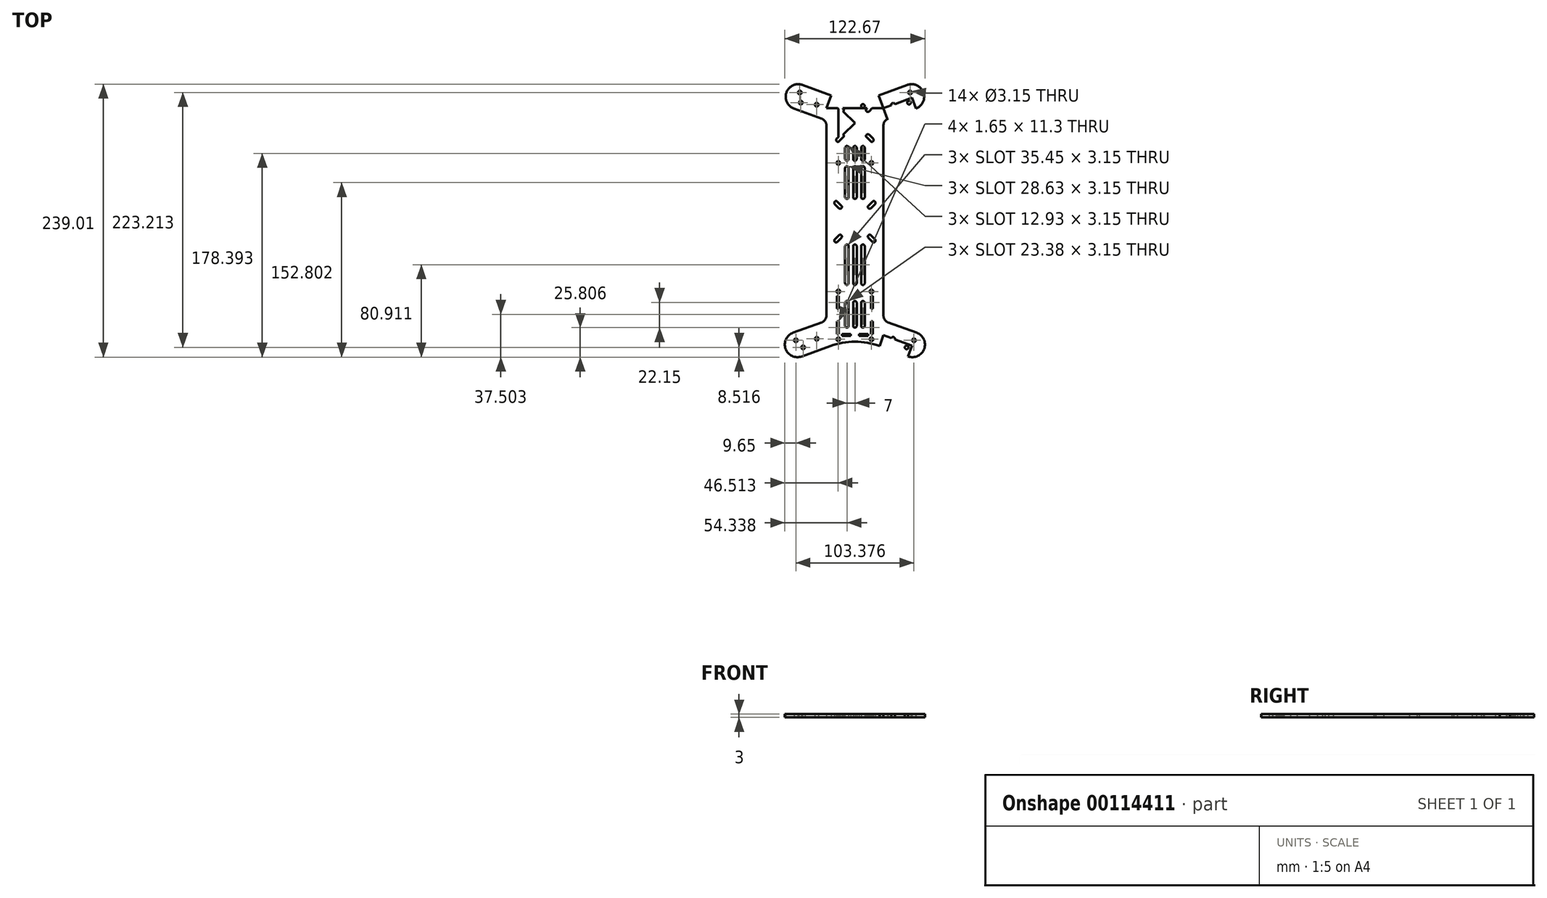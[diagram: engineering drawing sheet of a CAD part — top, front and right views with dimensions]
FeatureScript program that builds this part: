
annotation { "Feature Type Name" : "Feature", "Feature Type Description" : "" }
export const myFeature = defineFeature(function(context is Context, id is Id, definition is map)
    precondition{}
    {
        {
            var Q0;
            Q0=qCreatedBy(makeId("Top.planeOp"),FACE);
            var sketch = newSketch(context, id + "F0", { "sketchPlane" : qUnion([Q0])});
            skPoint(sketch, "E0.middle", {"position": v(0, 0) * mm});
            skLineSegment(sketch, "E1", {"start": v(4.78, 118.28) * mm, "end": v(4.78, 73.81) * mm});
            skCircle(sketch, "E2.MirrorC", {"center": v(56.47, -84.97) * mm, "radius": 1.57 * mm});
            skCircle(sketch, "E3.MirrorC", {"center": v(50.07, -91.17) * mm, "radius": 1.57 * mm});
            skCircle(sketch, "E4.MirrorC", {"center": v(38.24, -83.61) * mm, "radius": 1.57 * mm});
            skLineSegment(sketch, "E5", {"start": v(50.07, -91.17) * mm, "end": v(51.12, -88.3) * mm});
            skLineSegment(sketch, "E6", {"start": v(56.47, -84.97) * mm, "end": v(54.77, -89.63) * mm});
            skLineSegment(sketch, "E7", {"start": v(54.77, -89.63) * mm, "end": v(29.78, -80.53) * mm});
            skCircle(sketch, "E8.MirrorC", {"center": v(53.07, 132.04) * mm, "radius": 1.57 * mm});
            skCircle(sketch, "E9.MirrorC", {"center": v(52.16, 123.17) * mm, "radius": 1.57 * mm});
            skCircle(sketch, "E10.MirrorC", {"center": v(38.24, 121.36) * mm, "radius": 1.57 * mm});
            skLineSegment(sketch, "E11", {"start": v(52.16, 123.17) * mm, "end": v(51.12, 126.05) * mm});
            skLineSegment(sketch, "E12", {"start": v(50.67, 138.65) * mm, "end": v(53.07, 132.04) * mm});
            skLineSegment(sketch, "E13", {"start": v(54.77, 127.38) * mm, "end": v(29.78, 118.28) * mm});
            skLineSegment(sketch, "E14", {"start": v(29.78, 118.28) * mm, "end": v(4.78, 118.28) * mm});
            skLineSegment(sketch, "E15", {"start": v(29.78, -80.53) * mm, "end": v(4.78, -80.53) * mm});
            skLineSegment(sketch, "E16.bottom", {"start": v(21.28, 35.37) * mm, "end": v(4.78, 35.37) * mm});
            skLineSegment(sketch, "E16.top", {"start": v(21.28, 2.37) * mm, "end": v(4.78, 2.37) * mm});
            skLineSegment(sketch, "E16.left", {"start": v(21.28, 35.37) * mm, "end": v(21.28, 2.37) * mm});
            skLineSegment(sketch, "E17", {"start": v(29.78, 118.28) * mm, "end": v(29.78, -80.53) * mm});
            skCircle(sketch, "E18", {"center": v(21.28, 35.37) * mm, "radius": 1.58 * mm});
            skCircle(sketch, "E19", {"center": v(21.28, 2.37) * mm, "radius": 1.58 * mm});
            skLineSegment(sketch, "E20", {"start": v(4.78, 18.87) * mm, "end": v(21.28, 35.37) * mm});
            skLineSegment(sketch, "E21", {"start": v(4.78, 18.87) * mm, "end": v(21.28, 2.37) * mm});
            skPoint(sketch, "E22", {"position": v(17.74, 31.84) * mm});
            skPoint(sketch, "E23.MirrorP", {"position": v(17.74, 5.9) * mm});
            skCircle(sketch, "E24", {"center": v(17.74, 31.84) * mm, "radius": 1.58 * mm});
            skLineSegment(sketch, "E25", {"start": v(17.74, 31.84) * mm, "end": v(18.86, 30.72) * mm});
            skLineSegment(sketch, "E26", {"start": v(18.86, 30.72) * mm, "end": v(17.74, 31.84) * mm});
            skLineSegment(sketch, "E27", {"start": v(17.74, 31.84) * mm, "end": v(16.63, 32.95) * mm});
            skLineSegment(sketch, "E28", {"start": v(21.28, 35.37) * mm, "end": v(22.4, 34.26) * mm});
            skLineSegment(sketch, "E29", {"start": v(22.4, 34.26) * mm, "end": v(18.86, 30.72) * mm});
            skLineSegment(sketch, "E30", {"start": v(21.28, 35.37) * mm, "end": v(20.16, 36.49) * mm});
            skLineSegment(sketch, "E31", {"start": v(20.16, 36.49) * mm, "end": v(16.63, 32.95) * mm});
            skLineSegment(sketch, "E32", {"start": v(21.28, 2.37) * mm, "end": v(22.4, 3.49) * mm});
            skLineSegment(sketch, "E33", {"start": v(21.28, 2.37) * mm, "end": v(20.16, 1.26) * mm});
            skCircle(sketch, "E34", {"center": v(17.74, 5.9) * mm, "radius": 1.57 * mm});
            skLineSegment(sketch, "E35", {"start": v(17.74, 5.9) * mm, "end": v(16.63, 4.8) * mm});
            skLineSegment(sketch, "E36", {"start": v(16.63, 4.8) * mm, "end": v(20.16, 1.26) * mm});
            skLineSegment(sketch, "E37", {"start": v(17.74, 5.9) * mm, "end": v(18.86, 7.02) * mm});
            skLineSegment(sketch, "E38", {"start": v(18.86, 7.02) * mm, "end": v(22.4, 3.49) * mm});
            skLineSegment(sketch, "E39", {"start": v(58.87, -78.35) * mm, "end": v(33.88, -69.26) * mm});
            skLineSegment(sketch, "E40", {"start": v(51.35, -99.03) * mm, "end": v(26.36, -89.93) * mm});
            skLineSegment(sketch, "E41", {"start": v(33.88, -69.26) * mm, "end": v(29.78, -80.53) * mm});
            skLineSegment(sketch, "E42", {"start": v(29.78, -80.53) * mm, "end": v(26.36, -89.93) * mm});
            skLineSegment(sketch, "E43.MirrorCS", {"start": v(33.2, 108.88) * mm, "end": v(29.78, 118.28) * mm});
            skLineSegment(sketch, "E44", {"start": v(54.77, 127.38) * mm, "end": v(58.2, 117.98) * mm});
            skLineSegment(sketch, "E45", {"start": v(53.07, 132.04) * mm, "end": v(54.77, 127.38) * mm});
            skLineSegment(sketch, "E46", {"start": v(54.77, -89.63) * mm, "end": v(51.35, -99.03) * mm});
            skLineSegment(sketch, "E47", {"start": v(56.47, -84.97) * mm, "end": v(58.87, -78.35) * mm});
            skArc(sketch, "E48", {"start": v(51.35, -99.03) * mm, "mid": v(65.45, -92.45) * mm, "end": v(58.87, -78.35) * mm});
            skLineSegment(sketch, "E49.top", {"start": v(4.78, -46.08) * mm, "end": v(18.78, -46.08) * mm});
            skLineSegment(sketch, "E49.right", {"start": v(18.78, -79.53) * mm, "end": v(18.78, -46.08) * mm});
            skLineSegment(sketch, "E50", {"start": v(18.78, -46.08) * mm, "end": v(20.43, -46.08) * mm});
            skLineSegment(sketch, "E51", {"start": v(20.43, -46.08) * mm, "end": v(20.43, -57.38) * mm});
            skLineSegment(sketch, "E52", {"start": v(20.43, -57.38) * mm, "end": v(18.78, -57.38) * mm});
            skLineSegment(sketch, "E53.bottom", {"start": v(9.78, 110.28) * mm, "end": v(4.78, 110.28) * mm});
            skLineSegment(sketch, "E53.top", {"start": v(9.78, 100.28) * mm, "end": v(4.78, 100.28) * mm});
            skLineSegment(sketch, "E53.left", {"start": v(9.78, 110.28) * mm, "end": v(9.78, 100.28) * mm});
            skLineSegment(sketch, "E53.right", {"start": v(-0.22, 110.28) * mm, "end": v(-0.22, 100.28) * mm});
            skLineSegment(sketch, "E54", {"start": v(4.78, 105.28) * mm, "end": v(19.63, 120.13) * mm});
            skLineSegment(sketch, "E55", {"start": v(4.78, 105.28) * mm, "end": v(19.63, 90.43) * mm});
            skCircle(sketch, "E56", {"center": v(19.63, 120.13) * mm, "radius": 1.57 * mm});
            skCircle(sketch, "E57", {"center": v(19.63, 90.43) * mm, "radius": 1.57 * mm});
            skPoint(sketch, "E58", {"position": v(16.1, 116.6) * mm});
            skPoint(sketch, "E59", {"position": v(16.1, 93.97) * mm});
            skCircle(sketch, "E60", {"center": v(16.1, 116.6) * mm, "radius": 1.58 * mm});
            skLineSegment(sketch, "E61", {"start": v(19.63, 120.13) * mm, "end": v(20.74, 119.02) * mm});
            skLineSegment(sketch, "E62", {"start": v(19.63, 120.13) * mm, "end": v(18.51, 121.24) * mm});
            skLineSegment(sketch, "E63", {"start": v(16.1, 116.6) * mm, "end": v(17.2, 115.48) * mm});
            skLineSegment(sketch, "E64", {"start": v(17.2, 115.48) * mm, "end": v(20.74, 119.02) * mm});
            skLineSegment(sketch, "E65", {"start": v(16.1, 116.6) * mm, "end": v(14.98, 117.7) * mm});
            skLineSegment(sketch, "E66", {"start": v(14.98, 117.7) * mm, "end": v(18.51, 121.24) * mm});
            skCircle(sketch, "E67", {"center": v(16.1, 93.97) * mm, "radius": 1.58 * mm});
            skLineSegment(sketch, "E68", {"start": v(16.1, 93.97) * mm, "end": v(14.98, 92.85) * mm});
            skLineSegment(sketch, "E69", {"start": v(16.1, 93.97) * mm, "end": v(17.2, 95.08) * mm});
            skLineSegment(sketch, "E70", {"start": v(19.63, 90.43) * mm, "end": v(18.51, 89.32) * mm});
            skLineSegment(sketch, "E71", {"start": v(18.51, 89.32) * mm, "end": v(14.98, 92.85) * mm});
            skLineSegment(sketch, "E72", {"start": v(19.63, 90.43) * mm, "end": v(20.74, 91.55) * mm});
            skLineSegment(sketch, "E73", {"start": v(20.74, 91.55) * mm, "end": v(17.2, 95.08) * mm});
            skLineSegment(sketch, "E74", {"start": v(33.88, -69.26) * mm, "end": v(29.78, -67.76) * mm});
            skArc(sketch, "E75", {"start": v(33.88, -69.26) * mm, "mid": v(30.9, -66.97) * mm, "end": v(29.78, -63.4) * mm});
            skArc(sketch, "E76", {"start": v(26.36, -89.93) * mm, "mid": v(15.73, -87.08) * mm, "end": v(4.78, -86.13) * mm});
            skPoint(sketch, "E77", {"position": v(4.78, -86.13) * mm});
            skLineSegment(sketch, "E78", {"start": v(18.78, -68.23) * mm, "end": v(20.43, -68.23) * mm});
            skLineSegment(sketch, "E79", {"start": v(18.78, -79.53) * mm, "end": v(20.43, -79.53) * mm});
            skLineSegment(sketch, "E80", {"start": v(20.43, -79.53) * mm, "end": v(20.43, -68.23) * mm});
            skLineSegment(sketch, "E81", {"start": v(19.28, -79.53) * mm, "end": v(19.28, -84.03) * mm});
            skCircle(sketch, "E82", {"center": v(19.28, -84.03) * mm, "radius": 1.57 * mm});
            skLineSegment(sketch, "E83", {"start": v(19.28, -79.53) * mm, "end": v(19.28, -42.18) * mm});
            skCircle(sketch, "E84", {"center": v(19.28, -42.18) * mm, "radius": 1.57 * mm});
            skCircle(sketch, "E85.MirrorC", {"center": v(11.78, 120.28) * mm, "radius": 1.57 * mm});
            skLineSegment(sketch, "E86.MirrorCS", {"start": v(11.78, 118.28) * mm, "end": v(11.78, 120.28) * mm});
            skLineSegment(sketch, "E87", {"start": v(19.28, -42.18) * mm, "end": v(19.28, 118.28) * mm});
            skCircle(sketch, "E88", {"center": v(19.28, 70.37) * mm, "radius": 1.57 * mm});
            skLineSegment(sketch, "E89", {"start": v(4.78, -79.53) * mm, "end": v(4.78, -80.53) * mm});
            skLineSegment(sketch, "E90.trimOffspring", {"start": v(4.78, -79.53) * mm, "end": v(18.78, -79.53) * mm});
            skLineSegment(sketch, "E91.trimOffspring", {"start": v(4.78, 18.87) * mm, "end": v(29.78, 18.87) * mm});
            skLineSegment(sketch, "E92.MirrorCS", {"start": v(-8.19, 31.84) * mm, "end": v(-9.3, 30.72) * mm});
            skLineSegment(sketch, "E93.MirrorCS", {"start": v(-9.3, 30.72) * mm, "end": v(-8.19, 31.84) * mm});
            skLineSegment(sketch, "E94.MirrorCS", {"start": v(-11.72, 35.37) * mm, "end": v(-12.84, 34.26) * mm});
            skLineSegment(sketch, "E95.MirrorCS", {"start": v(-12.84, 34.26) * mm, "end": v(-9.3, 30.72) * mm});
            skLineSegment(sketch, "E96.MirrorCS", {"start": v(-11.72, 35.37) * mm, "end": v(-10.6, 36.49) * mm});
            skLineSegment(sketch, "E97.MirrorCS", {"start": v(-8.19, 31.84) * mm, "end": v(-7.07, 32.95) * mm});
            skCircle(sketch, "E98.MirrorC", {"center": v(-11.72, 35.37) * mm, "radius": 1.58 * mm});
            skLineSegment(sketch, "E99.MirrorCS", {"start": v(-10.6, 36.49) * mm, "end": v(-7.07, 32.95) * mm});
            skCircle(sketch, "E100.MirrorC", {"center": v(-8.19, 31.84) * mm, "radius": 1.58 * mm});
            skLineSegment(sketch, "E101.MirrorCS", {"start": v(-10.07, 120.13) * mm, "end": v(-11.18, 119.02) * mm});
            skLineSegment(sketch, "E102.MirrorCS", {"start": v(-10.07, 90.43) * mm, "end": v(-8.96, 89.32) * mm});
            skLineSegment(sketch, "E103.MirrorCS", {"start": v(-6.54, 93.97) * mm, "end": v(-7.65, 95.08) * mm});
            skLineSegment(sketch, "E104.MirrorCS", {"start": v(-6.54, 116.6) * mm, "end": v(-7.65, 115.48) * mm});
            skLineSegment(sketch, "E105.MirrorCS", {"start": v(-10.07, 120.13) * mm, "end": v(-8.96, 121.24) * mm});
            skLineSegment(sketch, "E106.MirrorCS", {"start": v(-11.72, 2.37) * mm, "end": v(-10.6, 1.26) * mm});
            skLineSegment(sketch, "E107.MirrorCS", {"start": v(-7.07, 4.8) * mm, "end": v(-10.6, 1.26) * mm});
            skLineSegment(sketch, "E108.MirrorCS", {"start": v(-11.72, 2.37) * mm, "end": v(-12.84, 3.49) * mm});
            skLineSegment(sketch, "E109.MirrorCS", {"start": v(-9.3, 7.02) * mm, "end": v(-12.84, 3.49) * mm});
            skCircle(sketch, "E110.MirrorC", {"center": v(-10.07, 120.13) * mm, "radius": 1.57 * mm});
            skCircle(sketch, "E111.MirrorC", {"center": v(-10.07, 90.43) * mm, "radius": 1.57 * mm});
            skLineSegment(sketch, "E112.MirrorCS", {"start": v(-5.42, 117.7) * mm, "end": v(-8.96, 121.24) * mm});
            skCircle(sketch, "E113.MirrorC", {"center": v(-11.72, 2.37) * mm, "radius": 1.58 * mm});
            skLineSegment(sketch, "E114.MirrorCS", {"start": v(-11.18, 91.55) * mm, "end": v(-7.65, 95.08) * mm});
            skLineSegment(sketch, "E115.MirrorCS", {"start": v(-8.96, 89.32) * mm, "end": v(-5.42, 92.85) * mm});
            skLineSegment(sketch, "E116.MirrorCS", {"start": v(-6.54, 116.6) * mm, "end": v(-5.42, 117.7) * mm});
            skLineSegment(sketch, "E117.MirrorCS", {"start": v(-9.22, -79.53) * mm, "end": v(-10.87, -79.53) * mm});
            skCircle(sketch, "E118.MirrorC", {"center": v(-6.54, 116.6) * mm, "radius": 1.58 * mm});
            skLineSegment(sketch, "E119.MirrorCS", {"start": v(-7.65, 115.48) * mm, "end": v(-11.18, 119.02) * mm});
            skLineSegment(sketch, "E120.MirrorCS", {"start": v(-6.54, 93.97) * mm, "end": v(-5.42, 92.85) * mm});
            skLineSegment(sketch, "E121.MirrorCS", {"start": v(-9.72, -79.53) * mm, "end": v(-9.72, -84.03) * mm});
            skCircle(sketch, "E122.MirrorC", {"center": v(-6.54, 93.97) * mm, "radius": 1.58 * mm});
            skLineSegment(sketch, "E123.MirrorCS", {"start": v(-10.07, 90.43) * mm, "end": v(-11.18, 91.55) * mm});
            skLineSegment(sketch, "E124.MirrorCS", {"start": v(-8.19, 5.9) * mm, "end": v(-9.3, 7.02) * mm});
            skLineSegment(sketch, "E125.MirrorCS", {"start": v(-42.6, 123.17) * mm, "end": v(-41.56, 126.05) * mm});
            skLineSegment(sketch, "E126.MirrorCS", {"start": v(-8.19, 5.9) * mm, "end": v(-7.07, 4.8) * mm});
            skLineSegment(sketch, "E127.MirrorCS", {"start": v(-24.33, -69.26) * mm, "end": v(-20.22, -67.76) * mm});
            skLineSegment(sketch, "E128.MirrorCS", {"start": v(-46.9, -84.97) * mm, "end": v(-45.21, -89.63) * mm});
            skCircle(sketch, "E129.MirrorC", {"center": v(-8.19, 5.9) * mm, "radius": 1.57 * mm});
            skLineSegment(sketch, "E130.MirrorCS", {"start": v(-40.51, -91.17) * mm, "end": v(-41.56, -88.3) * mm});
            skLineSegment(sketch, "E131.MirrorCS", {"start": v(-43.52, 132.04) * mm, "end": v(-45.21, 127.38) * mm});
            skLineSegment(sketch, "E132.MirrorCS", {"start": v(-24.33, -69.26) * mm, "end": v(-20.22, -80.53) * mm});
            skLineSegment(sketch, "E133.MirrorCS", {"start": v(-46.9, -84.97) * mm, "end": v(-49.32, -78.35) * mm});
            skCircle(sketch, "E134.MirrorC", {"center": v(-46.9, -84.97) * mm, "radius": 1.57 * mm});
            skLineSegment(sketch, "E135.MirrorCS", {"start": v(-2.22, 118.28) * mm, "end": v(-2.22, 120.28) * mm});
            skLineSegment(sketch, "E136.MirrorCS", {"start": v(-41.1, 138.65) * mm, "end": v(-43.52, 132.04) * mm});
            skLineSegment(sketch, "E137.MirrorCS", {"start": v(-23.64, 108.88) * mm, "end": v(-20.22, 118.28) * mm});
            skCircle(sketch, "E138.MirrorC", {"center": v(-43.52, 132.04) * mm, "radius": 1.57 * mm});
            skLineSegment(sketch, "E139.MirrorCS", {"start": v(-45.21, 127.38) * mm, "end": v(-48.63, 117.98) * mm});
            skLineSegment(sketch, "E140.MirrorCS", {"start": v(-20.22, 118.28) * mm, "end": v(-16.12, 129.56) * mm});
            skLineSegment(sketch, "E141.MirrorCS", {"start": v(-9.22, -79.53) * mm, "end": v(-9.22, -46.08) * mm});
            skLineSegment(sketch, "E142.MirrorCS", {"start": v(-10.87, -79.53) * mm, "end": v(-10.87, -68.23) * mm});
            skCircle(sketch, "E143.MirrorC", {"center": v(-2.22, 120.28) * mm, "radius": 1.57 * mm});
            skLineSegment(sketch, "E144.MirrorCS", {"start": v(-45.21, -89.63) * mm, "end": v(-41.8, -99.03) * mm});
            skLineSegment(sketch, "E145.MirrorCS", {"start": v(-20.22, -80.53) * mm, "end": v(-16.8, -89.93) * mm});
            skLineSegment(sketch, "E146.MirrorCS", {"start": v(-9.22, -68.23) * mm, "end": v(-10.87, -68.23) * mm});
            skLineSegment(sketch, "E147.MirrorCS", {"start": v(-9.22, -46.08) * mm, "end": v(-10.87, -46.08) * mm});
            skCircle(sketch, "E148.MirrorC", {"center": v(-42.6, 123.17) * mm, "radius": 1.57 * mm});
            skCircle(sketch, "E149.MirrorC", {"center": v(-40.51, -91.17) * mm, "radius": 1.57 * mm});
            skCircle(sketch, "E150.MirrorC", {"center": v(-9.72, -42.18) * mm, "radius": 1.57 * mm});
            skCircle(sketch, "E151.MirrorC", {"center": v(-9.72, -84.03) * mm, "radius": 1.57 * mm});
            skLineSegment(sketch, "E152.MirrorCS", {"start": v(-9.72, -79.53) * mm, "end": v(-9.72, -42.18) * mm});
            skArc(sketch, "E153.MirrorCS", {"start": v(-24.33, -69.26) * mm, "mid": v(-21.35, -66.97) * mm, "end": v(-20.22, -63.4) * mm});
            skLineSegment(sketch, "E154.MirrorCS", {"start": v(-10.87, -57.38) * mm, "end": v(-9.22, -57.38) * mm});
            skLineSegment(sketch, "E155.MirrorCS", {"start": v(-10.87, -46.08) * mm, "end": v(-10.87, -57.38) * mm});
            skCircle(sketch, "E156.MirrorC", {"center": v(-28.68, 121.36) * mm, "radius": 1.57 * mm});
            skCircle(sketch, "E157.MirrorC", {"center": v(-28.68, -83.61) * mm, "radius": 1.57 * mm});
            skLineSegment(sketch, "E158.MirrorCS", {"start": v(-45.21, -89.63) * mm, "end": v(-20.22, -80.53) * mm});
            skCircle(sketch, "E159.MirrorC", {"center": v(-9.72, 70.37) * mm, "radius": 1.57 * mm});
            skLineSegment(sketch, "E160.MirrorCS", {"start": v(-45.21, 127.38) * mm, "end": v(-20.22, 118.28) * mm});
            skLineSegment(sketch, "E161.MirrorCS", {"start": v(-41.8, -99.03) * mm, "end": v(-16.8, -89.93) * mm});
            skLineSegment(sketch, "E162.MirrorCS", {"start": v(-49.32, -78.35) * mm, "end": v(-24.33, -69.26) * mm});
            skArc(sketch, "E163.MirrorCS", {"start": v(-41.8, -99.03) * mm, "mid": v(-55.9, -92.45) * mm, "end": v(-49.32, -78.35) * mm});
            skLineSegment(sketch, "E164.MirrorCS", {"start": v(-20.22, 118.28) * mm, "end": v(-20.22, -80.53) * mm});
            skLineSegment(sketch, "E165.MirrorCS", {"start": v(-9.72, -42.18) * mm, "end": v(-9.72, 118.28) * mm});
            skLineSegment(sketch, "E166.MirrorCS", {"start": v(-11.72, 35.37) * mm, "end": v(-11.72, 2.37) * mm});
            skLineSegment(sketch, "E167.MirrorCS", {"start": v(-0.22, 110.28) * mm, "end": v(4.78, 110.28) * mm});
            skLineSegment(sketch, "E168.MirrorCS", {"start": v(-0.22, 100.28) * mm, "end": v(4.78, 100.28) * mm});
            skLineSegment(sketch, "E169.MirrorCS", {"start": v(4.78, 105.28) * mm, "end": v(-10.07, 90.43) * mm});
            skLineSegment(sketch, "E170.MirrorCS", {"start": v(4.78, 105.28) * mm, "end": v(-10.07, 120.13) * mm});
            skLineSegment(sketch, "E171.MirrorCS", {"start": v(-20.22, 118.28) * mm, "end": v(4.78, 118.28) * mm});
            skLineSegment(sketch, "E172.MirrorCS", {"start": v(-11.72, 35.37) * mm, "end": v(4.78, 35.37) * mm});
            skLineSegment(sketch, "E173.MirrorCS", {"start": v(-11.72, 2.37) * mm, "end": v(4.78, 2.37) * mm});
            skLineSegment(sketch, "E174.MirrorCS", {"start": v(4.78, 18.87) * mm, "end": v(-20.22, 18.87) * mm});
            skLineSegment(sketch, "E175.MirrorCS", {"start": v(4.78, 18.87) * mm, "end": v(-11.72, 35.37) * mm});
            skLineSegment(sketch, "E176.MirrorCS", {"start": v(4.78, 18.87) * mm, "end": v(-11.72, 2.37) * mm});
            skLineSegment(sketch, "E177.MirrorCS", {"start": v(4.78, -46.08) * mm, "end": v(-9.22, -46.08) * mm});
            skArc(sketch, "E178.MirrorCS", {"start": v(-16.8, -89.93) * mm, "mid": v(-6.18, -87.08) * mm, "end": v(4.78, -86.13) * mm});
            skLineSegment(sketch, "E179.MirrorCS", {"start": v(4.78, -79.53) * mm, "end": v(-9.22, -79.53) * mm});
            skLineSegment(sketch, "E180.MirrorCS", {"start": v(-20.22, -80.53) * mm, "end": v(4.78, -80.53) * mm});
            skLineSegment(sketch, "E181", {"start": v(16.2, -81.18) * mm, "end": v(8.55, -81.18) * mm});
            skLineSegment(sketch, "E182", {"start": v(1, -81.18) * mm, "end": v(-6.65, -81.18) * mm});
            skLineSegment(sketch, "E183", {"start": v(16.2, -81.18) * mm, "end": v(16.2, -79.53) * mm});
            skLineSegment(sketch, "E184", {"start": v(8.55, -81.18) * mm, "end": v(8.55, -79.53) * mm});
            skLineSegment(sketch, "E185", {"start": v(1, -81.18) * mm, "end": v(1, -79.53) * mm});
            skLineSegment(sketch, "E186", {"start": v(-6.65, -81.18) * mm, "end": v(-6.65, -79.53) * mm});
            skLineSegment(sketch, "E187", {"start": v(29.78, 118.28) * mm, "end": v(25.67, 129.56) * mm});
            skLineSegment(sketch, "E188", {"start": v(-41.1, 138.65) * mm, "end": v(-16.12, 129.56) * mm});
            skLineSegment(sketch, "E189", {"start": v(50.67, 138.65) * mm, "end": v(25.67, 129.56) * mm});
            skArc(sketch, "E190", {"start": v(25.67, 129.56) * mm, "mid": v(4.78, 125.87) * mm, "end": v(-16.12, 129.56) * mm});
            skLineSegment(sketch, "E191", {"start": v(58.2, 117.98) * mm, "end": v(33.88, 109.13) * mm});
            skLineSegment(sketch, "E192", {"start": v(-23.64, 108.88) * mm, "end": v(-48.63, 117.98) * mm});
            skLineSegment(sketch, "E193", {"start": v(-23.64, 108.88) * mm, "end": v(-20.22, 107.64) * mm});
            skLineSegment(sketch, "E194", {"start": v(33.2, 108.88) * mm, "end": v(29.78, 107.64) * mm});
            skArc(sketch, "E195", {"start": v(58.2, 117.98) * mm, "mid": v(64.76, 132.08) * mm, "end": v(50.67, 138.65) * mm});
            skArc(sketch, "E196", {"start": v(-48.63, 117.98) * mm, "mid": v(-55.2, 132.08) * mm, "end": v(-41.1, 138.65) * mm});
            skPoint(sketch, "E197", {"position": v(29.78, 103.27) * mm});
            skPoint(sketch, "E198", {"position": v(33.88, 109.13) * mm});
            skArc(sketch, "E199", {"start": v(33.88, 109.13) * mm, "mid": v(30.9, 106.85) * mm, "end": v(29.78, 103.27) * mm});
            skLineSegment(sketch, "E200", {"start": v(33.2, 108.88) * mm, "end": v(33.88, 109.13) * mm});
            skPoint(sketch, "E201.MirrorP", {"position": v(-24.33, 109.13) * mm});
            skPoint(sketch, "E202.MirrorP", {"position": v(-20.22, 103.27) * mm});
            skArc(sketch, "E203.MirrorCS", {"start": v(-24.33, 109.13) * mm, "mid": v(-21.35, 106.85) * mm, "end": v(-20.22, 103.27) * mm});
            skCircle(sketch, "E204", {"center": v(4.78, -2.63) * mm, "radius": 1.57 * mm});
            skCircle(sketch, "E205", {"center": v(4.78, -72.3) * mm, "radius": 1.57 * mm});
            skLineSegment(sketch, "E206", {"start": v(4.78, -72.3) * mm, "end": v(6.35, -72.3) * mm});
            skLineSegment(sketch, "E207", {"start": v(4.78, -72.3) * mm, "end": v(3.2, -72.3) * mm});
            skLineSegment(sketch, "E208", {"start": v(4.78, -2.63) * mm, "end": v(6.35, -2.63) * mm});
            skLineSegment(sketch, "E209", {"start": v(4.78, -2.63) * mm, "end": v(3.2, -2.63) * mm});
            skLineSegment(sketch, "E210", {"start": v(3.2, -2.63) * mm, "end": v(3.2, -34.93) * mm});
            skLineSegment(sketch, "E211", {"start": v(6.35, -72.3) * mm, "end": v(6.35, -52.07) * mm});
            skPoint(sketch, "E212", {"position": v(11.78, -46.08) * mm});
            skPoint(sketch, "E213", {"position": v(-2.22, -46.08) * mm});
            skLineSegment(sketch, "E214", {"start": v(6.35, -72.3) * mm, "end": v(11.78, -72.3) * mm});
            skLineSegment(sketch, "E215", {"start": v(11.78, -72.3) * mm, "end": v(11.78, -50.5) * mm});
            skLineSegment(sketch, "E216", {"start": v(3.2, -72.3) * mm, "end": v(-2.22, -72.3) * mm});
            skLineSegment(sketch, "E217", {"start": v(-2.22, -72.3) * mm, "end": v(-2.22, -50.5) * mm});
            skCircle(sketch, "E218", {"center": v(11.78, -72.3) * mm, "radius": 1.57 * mm});
            skCircle(sketch, "E219", {"center": v(-2.22, -72.3) * mm, "radius": 1.57 * mm});
            skLineSegment(sketch, "E220", {"start": v(11.78, -36.5) * mm, "end": v(11.78, -2.63) * mm});
            skLineSegment(sketch, "E221", {"start": v(-2.22, -36.5) * mm, "end": v(-2.22, -2.63) * mm});
            skCircle(sketch, "E222", {"center": v(-2.22, -2.63) * mm, "radius": 1.57 * mm});
            skCircle(sketch, "E223", {"center": v(11.78, -2.63) * mm, "radius": 1.57 * mm});
            skLineSegment(sketch, "E224", {"start": v(11.78, -2.63) * mm, "end": v(10.2, -2.63) * mm});
            skLineSegment(sketch, "E225", {"start": v(11.78, -2.63) * mm, "end": v(13.35, -2.63) * mm});
            skLineSegment(sketch, "E226", {"start": v(-2.22, -2.63) * mm, "end": v(-0.65, -2.63) * mm});
            skLineSegment(sketch, "E227", {"start": v(-2.22, -2.63) * mm, "end": v(-3.8, -2.63) * mm});
            skLineSegment(sketch, "E228", {"start": v(11.78, -72.3) * mm, "end": v(13.35, -72.3) * mm});
            skLineSegment(sketch, "E229", {"start": v(-2.22, -72.3) * mm, "end": v(-3.8, -72.3) * mm});
            skLineSegment(sketch, "E230", {"start": v(-3.8, -72.3) * mm, "end": v(-3.8, -52.07) * mm});
            skLineSegment(sketch, "E231", {"start": v(-0.65, -2.63) * mm, "end": v(-0.65, -34.93) * mm});
            skLineSegment(sketch, "E232", {"start": v(10.2, -72.3) * mm, "end": v(10.2, -52.07) * mm});
            skLineSegment(sketch, "E233", {"start": v(13.35, -2.63) * mm, "end": v(13.35, -34.93) * mm});
            skCircle(sketch, "E234", {"center": v(4.78, 40.37) * mm, "radius": 1.57 * mm});
            skLineSegment(sketch, "E235", {"start": v(-9.72, 83.6) * mm, "end": v(19.28, 83.6) * mm});
            skLineSegment(sketch, "E236", {"start": v(-2.22, -2.63) * mm, "end": v(-2.22, 65.85) * mm});
            skLineSegment(sketch, "E237", {"start": v(11.78, -2.63) * mm, "end": v(11.78, 65.85) * mm});
            skLineSegment(sketch, "E238", {"start": v(4.78, 40.37) * mm, "end": v(11.78, 40.37) * mm});
            skLineSegment(sketch, "E239", {"start": v(11.78, 40.37) * mm, "end": v(19.28, 40.37) * mm});
            skLineSegment(sketch, "E240", {"start": v(4.78, 40.37) * mm, "end": v(-2.22, 40.37) * mm});
            skLineSegment(sketch, "E241", {"start": v(-2.22, 40.37) * mm, "end": v(-9.72, 40.37) * mm});
            skCircle(sketch, "E242", {"center": v(-2.22, 40.37) * mm, "radius": 1.57 * mm});
            skCircle(sketch, "E243", {"center": v(11.78, 40.37) * mm, "radius": 1.57 * mm});
            skCircle(sketch, "E244", {"center": v(4.78, 83.6) * mm, "radius": 1.57 * mm});
            skCircle(sketch, "E245", {"center": v(11.78, 83.6) * mm, "radius": 1.57 * mm});
            skCircle(sketch, "E246", {"center": v(-2.22, 83.6) * mm, "radius": 1.57 * mm});
            skLineSegment(sketch, "E247", {"start": v(-3.8, 83.6) * mm, "end": v(-3.8, 73.81) * mm});
            skLineSegment(sketch, "E248", {"start": v(-0.65, 40.37) * mm, "end": v(-0.65, 65.85) * mm});
            skLineSegment(sketch, "E249", {"start": v(3.2, 83.6) * mm, "end": v(3.2, 73.81) * mm});
            skLineSegment(sketch, "E250", {"start": v(6.35, 40.37) * mm, "end": v(6.35, 65.85) * mm});
            skLineSegment(sketch, "E251", {"start": v(10.2, 83.6) * mm, "end": v(10.2, 73.81) * mm});
            skLineSegment(sketch, "E252", {"start": v(13.35, 40.37) * mm, "end": v(13.35, 65.85) * mm});
            skLineSegment(sketch, "E253", {"start": v(-3.8, -34.93) * mm, "end": v(13.35, -34.93) * mm});
            skLineSegment(sketch, "E254", {"start": v(-3.8, -52.07) * mm, "end": v(13.35, -52.07) * mm});
            skCircle(sketch, "E255", {"center": v(-2.22, -34.93) * mm, "radius": 1.57 * mm});
            skCircle(sketch, "E256", {"center": v(4.78, -34.93) * mm, "radius": 1.58 * mm});
            skCircle(sketch, "E257", {"center": v(11.78, -34.93) * mm, "radius": 1.57 * mm});
            skCircle(sketch, "E258", {"center": v(-2.22, -52.07) * mm, "radius": 1.57 * mm});
            skCircle(sketch, "E259", {"center": v(4.78, -52.07) * mm, "radius": 1.58 * mm});
            skCircle(sketch, "E260", {"center": v(11.78, -52.07) * mm, "radius": 1.57 * mm});
            skLineSegment(sketch, "E261.trimOffspring", {"start": v(-3.8, -34.93) * mm, "end": v(-3.8, -2.63) * mm});
            skLineSegment(sketch, "E262.trimOffspring", {"start": v(-0.65, -52.07) * mm, "end": v(-0.65, -72.3) * mm});
            skLineSegment(sketch, "E263.trimOffspring", {"start": v(3.2, -52.07) * mm, "end": v(3.2, -72.3) * mm});
            skLineSegment(sketch, "E264.trimOffspring", {"start": v(6.35, -34.93) * mm, "end": v(6.35, -2.63) * mm});
            skLineSegment(sketch, "E265.trimOffspring", {"start": v(10.2, -34.93) * mm, "end": v(10.2, -2.63) * mm});
            skLineSegment(sketch, "E266.trimOffspring", {"start": v(13.35, -52.07) * mm, "end": v(13.35, -72.3) * mm});
            skLineSegment(sketch, "E267", {"start": v(-3.8, 73.81) * mm, "end": v(13.35, 73.81) * mm});
            skLineSegment(sketch, "E268", {"start": v(-3.8, 65.85) * mm, "end": v(13.35, 65.85) * mm});
            skLineSegment(sketch, "E269.trimOffspring", {"start": v(-3.8, 65.85) * mm, "end": v(-3.8, 40.37) * mm});
            skLineSegment(sketch, "E270.trimOffspring", {"start": v(-2.22, 73.81) * mm, "end": v(-2.22, 83.6) * mm});
            skLineSegment(sketch, "E271.trimOffspring", {"start": v(-0.65, 73.81) * mm, "end": v(-0.65, 83.6) * mm});
            skLineSegment(sketch, "E272.trimOffspring", {"start": v(3.2, 65.85) * mm, "end": v(3.2, 40.37) * mm});
            skLineSegment(sketch, "E273.trimOffspring", {"start": v(4.78, 65.85) * mm, "end": v(4.78, -79.53) * mm});
            skLineSegment(sketch, "E274.trimOffspring", {"start": v(6.35, 73.81) * mm, "end": v(6.35, 83.6) * mm});
            skLineSegment(sketch, "E275.trimOffspring", {"start": v(10.2, 65.85) * mm, "end": v(10.2, 40.37) * mm});
            skLineSegment(sketch, "E276.trimOffspring", {"start": v(13.35, 73.81) * mm, "end": v(13.35, 83.6) * mm});
            skCircle(sketch, "E277", {"center": v(-2.22, 73.81) * mm, "radius": 1.57 * mm});
            skCircle(sketch, "E278", {"center": v(4.78, 73.81) * mm, "radius": 1.57 * mm});
            skLineSegment(sketch, "E279.trimOffspring", {"start": v(11.78, 73.81) * mm, "end": v(11.78, 83.6) * mm});
            skCircle(sketch, "E280", {"center": v(11.78, 73.81) * mm, "radius": 1.57 * mm});
            skCircle(sketch, "E281", {"center": v(-2.22, 65.85) * mm, "radius": 1.57 * mm});
            skCircle(sketch, "E282", {"center": v(4.78, 65.85) * mm, "radius": 1.57 * mm});
            skCircle(sketch, "E283", {"center": v(11.78, 65.85) * mm, "radius": 1.57 * mm});
            skSolve(sketch);
        }
        {
            var Q0;
            {var subQ0=sQuery(id+"F0.wireOp",EDGE,"E210");var subQ1=sQuery(id+"F0.wireOp",EDGE,"E177.MirrorCS");var subQ2=makeQuery(id+"F0.imprint","INTERSECT",VERTEX,{"derivedFrom":[subQ1,subQ0]});Q0=makeQuery(id+"F0.imprint","IMPRINT",FACE,{"disambiguationData":[TD([[makeQuery(id+"F0.imprint","IMPRINT",EDGE,{"disambiguationData":[TD([[subQ2,-1.0]])],"derivedFrom":subQ1}),1.0]])]});}
            var Q1;
            {var subQ0=sQuery(id+"F0.wireOp",EDGE,"E89");Q1=makeQuery(id+"F0.imprint","IMPRINT",FACE,{"disambiguationData":[TD([[makeQuery(id+"F0.imprint","IMPRINT",EDGE,{"derivedFrom":subQ0}),1.0]])]});}
            var Q2;
            {var subQ5=sQuery(id+"F0.wireOp",EDGE,"E44");Q2=makeQuery(id+"F0.imprint","IMPRINT",FACE,{"disambiguationData":[TD([[makeQuery(id+"F0.imprint","IMPRINT",EDGE,{"derivedFrom":subQ5}),1.0]])]});}
            var Q3;
            Q3=makeQuery(id+"F0.imprint","IMPRINT",FACE,{"disambiguationData":[TD([[makeQuery(id+"F0.imprint","IMPRINT",EDGE,{"derivedFrom":sQuery(id+"F0.wireOp",EDGE,"E9.MirrorC")}),1.0]])]});
            var Q4;
            {var subQ0=sQuery(id+"F0.wireOp",EDGE,"E43.MirrorCS");Q4=makeQuery(id+"F0.imprint","IMPRINT",FACE,{"disambiguationData":[TD([[makeQuery(id+"F0.imprint","IMPRINT",EDGE,{"derivedFrom":subQ0}),1.0]])]});}
            var Q5;
            {var subQ6=sQuery(id+"F0.wireOp",EDGE,"E53.left");Q5=makeQuery(id+"F0.imprint","IMPRINT",FACE,{"disambiguationData":[TD([[makeQuery(id+"F0.imprint","IMPRINT",EDGE,{"derivedFrom":subQ6}),1.0]])]});}
            var Q6;
            {var subQ10=sQuery(id+"F0.wireOp",EDGE,"E53.bottom");Q6=makeQuery(id+"F0.imprint","IMPRINT",FACE,{"disambiguationData":[TD([[makeQuery(id+"F0.imprint","IMPRINT",EDGE,{"derivedFrom":subQ10}),-1.0]])]});}
            var Q7;
            {var subQ10=sQuery(id+"F0.wireOp",EDGE,"E53.bottom");Q7=makeQuery(id+"F0.imprint","IMPRINT",FACE,{"disambiguationData":[TD([[makeQuery(id+"F0.imprint","IMPRINT",EDGE,{"derivedFrom":subQ10}),-1.0]])]});}
            var Q8;
            {var subQ0=sQuery(id+"F0.wireOp",EDGE,"E53.bottom");Q8=makeQuery(id+"F0.imprint","IMPRINT",FACE,{"disambiguationData":[TD([[makeQuery(id+"F0.imprint","IMPRINT",EDGE,{"derivedFrom":subQ0}),1.0]])]});}
            var Q9;
            {var subQ0=sQuery(id+"F0.wireOp",EDGE,"E53.bottom");Q9=makeQuery(id+"F0.imprint","IMPRINT",FACE,{"disambiguationData":[TD([[makeQuery(id+"F0.imprint","IMPRINT",EDGE,{"derivedFrom":subQ0}),1.0]])]});}
            var Q10;
            {var subQ0=sQuery(id+"F0.wireOp",EDGE,"E53.left");Q10=makeQuery(id+"F0.imprint","IMPRINT",FACE,{"disambiguationData":[TD([[makeQuery(id+"F0.imprint","IMPRINT",EDGE,{"derivedFrom":subQ0}),-1.0]])]});}
            var Q11;
            {var subQ0=sQuery(id+"F0.wireOp",EDGE,"E53.top");Q11=makeQuery(id+"F0.imprint","IMPRINT",FACE,{"disambiguationData":[TD([[makeQuery(id+"F0.imprint","IMPRINT",EDGE,{"derivedFrom":subQ0}),-1.0]])]});}
            var Q12;
            {var subQ0=sQuery(id+"F0.wireOp",EDGE,"E53.top");Q12=makeQuery(id+"F0.imprint","IMPRINT",FACE,{"disambiguationData":[TD([[makeQuery(id+"F0.imprint","IMPRINT",EDGE,{"derivedFrom":subQ0}),-1.0]])]});}
            var Q13;
            {var subQ15=sQuery(id+"F0.wireOp",EDGE,"E53.top");Q13=makeQuery(id+"F0.imprint","IMPRINT",FACE,{"disambiguationData":[TD([[makeQuery(id+"F0.imprint","IMPRINT",EDGE,{"derivedFrom":subQ15}),1.0]])]});}
            var Q14;
            {var subQ0=sQuery(id+"F0.wireOp",EDGE,"E31");var subQ7=sQuery(id+"F0.wireOp",EDGE,"E16.bottom");var subQ8=makeQuery(id+"F0.imprint","INTERSECT",VERTEX,{"derivedFrom":[subQ7,subQ0]});Q14=makeQuery(id+"F0.imprint","IMPRINT",FACE,{"disambiguationData":[TD([[makeQuery(id+"F0.imprint","IMPRINT",EDGE,{"disambiguationData":[TD([[subQ8,-1.0]])],"derivedFrom":subQ7}),1.0]])]});}
            var Q15;
            {var subQ0=sQuery(id+"F0.wireOp",EDGE,"E36");var subQ5=sQuery(id+"F0.wireOp",EDGE,"E16.top");var subQ8=makeQuery(id+"F0.imprint","INTERSECT",VERTEX,{"derivedFrom":[subQ5,subQ0]});Q15=makeQuery(id+"F0.imprint","IMPRINT",FACE,{"disambiguationData":[TD([[makeQuery(id+"F0.imprint","IMPRINT",EDGE,{"disambiguationData":[TD([[subQ8,-1.0]])],"derivedFrom":subQ5}),-1.0]])]});}
            var Q16;
            {var subQ13=sQuery(id+"F0.wireOp",EDGE,"E51");Q16=makeQuery(id+"F0.imprint","IMPRINT",FACE,{"disambiguationData":[TD([[makeQuery(id+"F0.imprint","IMPRINT",EDGE,{"derivedFrom":subQ13}),1.0]])]});}
            var Q17;
            {var subQ15=sQuery(id+"F0.wireOp",EDGE,"E16.top");var subQ20=sQuery(id+"F0.wireOp",EDGE,"E36");var subQ21=makeQuery(id+"F0.imprint","INTERSECT",VERTEX,{"derivedFrom":[subQ15,subQ20]});Q17=makeQuery(id+"F0.imprint","IMPRINT",FACE,{"disambiguationData":[TD([[makeQuery(id+"F0.imprint","IMPRINT",EDGE,{"disambiguationData":[TD([[subQ21,-1.0]])],"derivedFrom":subQ20}),-1.0]])]});}
            var Q18;
            {var subQ9=sQuery(id+"F0.wireOp",EDGE,"E173.MirrorCS");var subQ11=sQuery(id+"F0.wireOp",EDGE,"E107.MirrorCS");var subQ12=makeQuery(id+"F0.imprint","INTERSECT",VERTEX,{"derivedFrom":[subQ11,subQ9]});Q18=makeQuery(id+"F0.imprint","IMPRINT",FACE,{"disambiguationData":[TD([[makeQuery(id+"F0.imprint","IMPRINT",EDGE,{"disambiguationData":[TD([[subQ12,-1.0]])],"derivedFrom":subQ11}),1.0]])]});}
            var Q19;
            {var subQ0=sQuery(id+"F0.wireOp",EDGE,"E168.MirrorCS");Q19=makeQuery(id+"F0.imprint","IMPRINT",FACE,{"disambiguationData":[TD([[makeQuery(id+"F0.imprint","IMPRINT",EDGE,{"derivedFrom":subQ0}),1.0]])]});}
            var Q20;
            {var subQ0=sQuery(id+"F0.wireOp",EDGE,"E53.top");Q20=makeQuery(id+"F0.imprint","IMPRINT",FACE,{"disambiguationData":[TD([[makeQuery(id+"F0.imprint","IMPRINT",EDGE,{"derivedFrom":subQ0}),-1.0]])]});}
            var Q21;
            {var subQ9=sQuery(id+"F0.wireOp",EDGE,"E42");Q21=makeQuery(id+"F0.imprint","IMPRINT",FACE,{"disambiguationData":[TD([[makeQuery(id+"F0.imprint","IMPRINT",EDGE,{"derivedFrom":subQ9}),-1.0]])]});}
            var Q22;
            {var subQ0=sQuery(id+"F0.wireOp",EDGE,"E74");Q22=makeQuery(id+"F0.imprint","IMPRINT",FACE,{"disambiguationData":[TD([[makeQuery(id+"F0.imprint","IMPRINT",EDGE,{"derivedFrom":subQ0}),-1.0]])]});}
            var Q23;
            {var subQ0=sQuery(id+"F0.wireOp",EDGE,"E41");Q23=makeQuery(id+"F0.imprint","IMPRINT",FACE,{"disambiguationData":[TD([[makeQuery(id+"F0.imprint","IMPRINT",EDGE,{"derivedFrom":subQ0}),-1.0]])]});}
            var Q24;
            Q24=makeQuery(id+"F0.imprint","IMPRINT",FACE,{"disambiguationData":[TD([[makeQuery(id+"F0.imprint","IMPRINT",EDGE,{"derivedFrom":sQuery(id+"F0.wireOp",EDGE,"E3.MirrorC")}),1.0]])]});
            var Q25;
            {var subQ6=sQuery(id+"F0.wireOp",EDGE,"E39");Q25=makeQuery(id+"F0.imprint","IMPRINT",FACE,{"disambiguationData":[TD([[makeQuery(id+"F0.imprint","IMPRINT",EDGE,{"derivedFrom":subQ6}),1.0]])]});}
            var Q26;
            {var subQ4=sQuery(id+"F0.wireOp",EDGE,"E46");Q26=makeQuery(id+"F0.imprint","IMPRINT",FACE,{"disambiguationData":[TD([[makeQuery(id+"F0.imprint","IMPRINT",EDGE,{"derivedFrom":subQ4}),1.0]])]});}
            var Q27;
            {var subQ0=sQuery(id+"F0.wireOp",EDGE,"E89");Q27=makeQuery(id+"F0.imprint","IMPRINT",FACE,{"disambiguationData":[TD([[makeQuery(id+"F0.imprint","IMPRINT",EDGE,{"derivedFrom":subQ0}),1.0]])]});}
            var Q28;
            {var subQ0=sQuery(id+"F0.wireOp",EDGE,"E81");var subQ3=sQuery(id+"F0.wireOp",EDGE,"E15");var subQ4=makeQuery(id+"F0.imprint","INTERSECT",VERTEX,{"derivedFrom":[subQ3,subQ0]});Q28=makeQuery(id+"F0.imprint","IMPRINT",FACE,{"disambiguationData":[TD([[makeQuery(id+"F0.imprint","IMPRINT",EDGE,{"disambiguationData":[TD([[subQ4,-1.0]])],"derivedFrom":subQ3}),-1.0]])]});}
            var Q29;
            {var subQ0=sQuery(id+"F0.wireOp",EDGE,"E52");var subQ1=sQuery(id+"F0.wireOp",EDGE,"E49.right");var subQ2=makeQuery(id+"F0.imprint","INTERSECT",VERTEX,{"derivedFrom":[subQ1,subQ0]});Q29=makeQuery(id+"F0.imprint","IMPRINT",FACE,{"disambiguationData":[TD([[makeQuery(id+"F0.imprint","IMPRINT",EDGE,{"disambiguationData":[TD([[subQ2,1.0]])],"derivedFrom":subQ1}),-1.0]])]});}
            var Q30;
            {var subQ6=sQuery(id+"F0.wireOp",EDGE,"E137.MirrorCS");Q30=makeQuery(id+"F0.imprint","IMPRINT",FACE,{"disambiguationData":[TD([[makeQuery(id+"F0.imprint","IMPRINT",EDGE,{"derivedFrom":subQ6}),1.0]])]});}
            var Q31;
            {var subQ8=sQuery(id+"F0.wireOp",EDGE,"E140.MirrorCS");Q31=makeQuery(id+"F0.imprint","IMPRINT",FACE,{"disambiguationData":[TD([[makeQuery(id+"F0.imprint","IMPRINT",EDGE,{"derivedFrom":subQ8}),1.0]])]});}
            var Q32;
            {var subQ0=sQuery(id+"F0.wireOp",EDGE,"E139.MirrorCS");Q32=makeQuery(id+"F0.imprint","IMPRINT",FACE,{"disambiguationData":[TD([[makeQuery(id+"F0.imprint","IMPRINT",EDGE,{"derivedFrom":subQ0}),-1.0]])]});}
            var Q33;
            {var subQ7=sQuery(id+"F0.wireOp",EDGE,"E165.MirrorCS");var subQ13=sQuery(id+"F0.wireOp",EDGE,"E119.MirrorCS");var subQ15=makeQuery(id+"F0.imprint","INTERSECT",VERTEX,{"derivedFrom":[subQ13,subQ7]});Q33=makeQuery(id+"F0.imprint","IMPRINT",FACE,{"disambiguationData":[TD([[makeQuery(id+"F0.imprint","IMPRINT",EDGE,{"disambiguationData":[TD([[subQ15,-1.0]])],"derivedFrom":subQ13}),1.0]])]});}
            var Q34;
            {var subQ13=sQuery(id+"F0.wireOp",EDGE,"E53.right");Q34=makeQuery(id+"F0.imprint","IMPRINT",FACE,{"disambiguationData":[TD([[makeQuery(id+"F0.imprint","IMPRINT",EDGE,{"derivedFrom":subQ13}),-1.0]])]});}
            var Q35;
            {var subQ7=sQuery(id+"F0.wireOp",EDGE,"E167.MirrorCS");Q35=makeQuery(id+"F0.imprint","IMPRINT",FACE,{"disambiguationData":[TD([[makeQuery(id+"F0.imprint","IMPRINT",EDGE,{"derivedFrom":subQ7}),1.0]])]});}
            var Q36;
            {var subQ9=sQuery(id+"F0.wireOp",EDGE,"E29");var subQ12=sQuery(id+"F0.wireOp",EDGE,"E16.left");var subQ13=makeQuery(id+"F0.imprint","INTERSECT",VERTEX,{"derivedFrom":[subQ12,subQ9]});Q36=makeQuery(id+"F0.imprint","IMPRINT",FACE,{"disambiguationData":[TD([[makeQuery(id+"F0.imprint","IMPRINT",EDGE,{"disambiguationData":[TD([[subQ13,-1.0]])],"derivedFrom":subQ12}),1.0]])]});}
            var Q37;
            {var subQ16=sQuery(id+"F0.wireOp",EDGE,"E115.MirrorCS");Q37=makeQuery(id+"F0.imprint","IMPRINT",FACE,{"disambiguationData":[TD([[makeQuery(id+"F0.imprint","IMPRINT",EDGE,{"derivedFrom":subQ16}),-1.0]])]});}
            var Q38;
            {var subQ0=sQuery(id+"F0.wireOp",EDGE,"E167.MirrorCS");Q38=makeQuery(id+"F0.imprint","IMPRINT",FACE,{"disambiguationData":[TD([[makeQuery(id+"F0.imprint","IMPRINT",EDGE,{"derivedFrom":subQ0}),-1.0]])]});}
            var Q39;
            {var subQ0=sQuery(id+"F0.wireOp",EDGE,"E53.right");Q39=makeQuery(id+"F0.imprint","IMPRINT",FACE,{"disambiguationData":[TD([[makeQuery(id+"F0.imprint","IMPRINT",EDGE,{"derivedFrom":subQ0}),1.0]])]});}
            var Q40;
            {var subQ0=sQuery(id+"F0.wireOp",EDGE,"E172.MirrorCS");var subQ3=sQuery(id+"F0.wireOp",EDGE,"E99.MirrorCS");var subQ4=makeQuery(id+"F0.imprint","INTERSECT",VERTEX,{"derivedFrom":[subQ3,subQ0]});Q40=makeQuery(id+"F0.imprint","IMPRINT",FACE,{"disambiguationData":[TD([[makeQuery(id+"F0.imprint","IMPRINT",EDGE,{"disambiguationData":[TD([[subQ4,-1.0]])],"derivedFrom":subQ3}),1.0]])]});}
            var Q41;
            {var subQ3=sQuery(id+"F0.wireOp",EDGE,"E165.MirrorCS");var subQ6=sQuery(id+"F0.wireOp",EDGE,"E95.MirrorCS");var subQ8=makeQuery(id+"F0.imprint","INTERSECT",VERTEX,{"derivedFrom":[subQ6,subQ3]});Q41=makeQuery(id+"F0.imprint","IMPRINT",FACE,{"disambiguationData":[TD([[makeQuery(id+"F0.imprint","IMPRINT",EDGE,{"disambiguationData":[TD([[subQ8,1.0]])],"derivedFrom":subQ3}),-1.0]])]});}
            var Q42;
            {var subQ0=sQuery(id+"F0.wireOp",EDGE,"E165.MirrorCS");var subQ1=sQuery(id+"F0.wireOp",EDGE,"E109.MirrorCS");var subQ2=makeQuery(id+"F0.imprint","INTERSECT",VERTEX,{"derivedFrom":[subQ1,subQ0]});Q42=makeQuery(id+"F0.imprint","IMPRINT",FACE,{"disambiguationData":[TD([[makeQuery(id+"F0.imprint","IMPRINT",EDGE,{"disambiguationData":[TD([[subQ2,-1.0]])],"derivedFrom":subQ0}),-1.0]])]});}
            var Q43;
            {var subQ1=sQuery(id+"F0.wireOp",EDGE,"E107.MirrorCS");var subQ5=sQuery(id+"F0.wireOp",EDGE,"E173.MirrorCS");var subQ9=makeQuery(id+"F0.imprint","INTERSECT",VERTEX,{"derivedFrom":[subQ1,subQ5]});Q43=makeQuery(id+"F0.imprint","IMPRINT",FACE,{"disambiguationData":[TD([[makeQuery(id+"F0.imprint","IMPRINT",EDGE,{"disambiguationData":[TD([[subQ9,1.0]])],"derivedFrom":subQ1}),1.0]])]});}
            var Q44;
            {var subQ0=sQuery(id+"F0.wireOp",EDGE,"E29");var subQ3=sQuery(id+"F0.wireOp",EDGE,"E87");var subQ4=makeQuery(id+"F0.imprint","INTERSECT",VERTEX,{"derivedFrom":[subQ0,subQ3]});Q44=makeQuery(id+"F0.imprint","IMPRINT",FACE,{"disambiguationData":[TD([[makeQuery(id+"F0.imprint","IMPRINT",EDGE,{"disambiguationData":[TD([[subQ4,1.0]])],"derivedFrom":subQ3}),1.0]])]});}
            var Q45;
            {var subQ0=sQuery(id+"F0.wireOp",EDGE,"E87");var subQ1=sQuery(id+"F0.wireOp",EDGE,"E38");var subQ2=makeQuery(id+"F0.imprint","INTERSECT",VERTEX,{"derivedFrom":[subQ1,subQ0]});Q45=makeQuery(id+"F0.imprint","IMPRINT",FACE,{"disambiguationData":[TD([[makeQuery(id+"F0.imprint","IMPRINT",EDGE,{"disambiguationData":[TD([[subQ2,-1.0]])],"derivedFrom":subQ0}),1.0]])]});}
            var Q46;
            {var subQ0=sQuery(id+"F0.wireOp",EDGE,"E29");var subQ1=sQuery(id+"F0.wireOp",EDGE,"E16.left");var subQ2=makeQuery(id+"F0.imprint","INTERSECT",VERTEX,{"derivedFrom":[subQ1,subQ0]});Q46=makeQuery(id+"F0.imprint","IMPRINT",FACE,{"disambiguationData":[TD([[makeQuery(id+"F0.imprint","IMPRINT",EDGE,{"disambiguationData":[TD([[subQ2,-1.0]])],"derivedFrom":subQ1}),-1.0]])]});}
            var Q47;
            {var subQ0=sQuery(id+"F0.wireOp",EDGE,"E91.trimOffspring");var subQ1=sQuery(id+"F0.wireOp",EDGE,"E16.left");var subQ2=makeQuery(id+"F0.imprint","INTERSECT",VERTEX,{"derivedFrom":[subQ1,subQ0]});Q47=makeQuery(id+"F0.imprint","IMPRINT",FACE,{"disambiguationData":[TD([[makeQuery(id+"F0.imprint","IMPRINT",EDGE,{"disambiguationData":[TD([[subQ2,-1.0]])],"derivedFrom":subQ1}),-1.0]])]});}
            var Q48;
            {var subQ0=sQuery(id+"F0.wireOp",EDGE,"E165.MirrorCS");var subQ1=sQuery(id+"F0.wireOp",EDGE,"E109.MirrorCS");var subQ2=makeQuery(id+"F0.imprint","INTERSECT",VERTEX,{"derivedFrom":[subQ1,subQ0]});Q48=makeQuery(id+"F0.imprint","IMPRINT",FACE,{"disambiguationData":[TD([[makeQuery(id+"F0.imprint","IMPRINT",EDGE,{"disambiguationData":[TD([[subQ2,-1.0]])],"derivedFrom":subQ1}),-1.0]])]});}
            var Q49;
            {var subQ0=sQuery(id+"F0.wireOp",EDGE,"E166.MirrorCS");var subQ1=sQuery(id+"F0.wireOp",EDGE,"E95.MirrorCS");var subQ2=makeQuery(id+"F0.imprint","INTERSECT",VERTEX,{"derivedFrom":[subQ1,subQ0]});Q49=makeQuery(id+"F0.imprint","IMPRINT",FACE,{"disambiguationData":[TD([[makeQuery(id+"F0.imprint","IMPRINT",EDGE,{"disambiguationData":[TD([[subQ2,-1.0]])],"derivedFrom":subQ1}),-1.0]])]});}
            var Q50;
            {var subQ0=sQuery(id+"F0.wireOp",EDGE,"E211");var subQ1=sQuery(id+"F0.wireOp",EDGE,"E49.top");var subQ2=makeQuery(id+"F0.imprint","INTERSECT",VERTEX,{"derivedFrom":[subQ1,subQ0]});Q50=makeQuery(id+"F0.imprint","IMPRINT",FACE,{"disambiguationData":[TD([[makeQuery(id+"F0.imprint","IMPRINT",EDGE,{"disambiguationData":[TD([[subQ2,-1.0]])],"derivedFrom":subQ1}),-1.0]])]});}
            var Q51;
            {var subQ6=sQuery(id+"F0.wireOp",EDGE,"E132.MirrorCS");Q51=makeQuery(id+"F0.imprint","IMPRINT",FACE,{"disambiguationData":[TD([[makeQuery(id+"F0.imprint","IMPRINT",EDGE,{"derivedFrom":subQ6}),-1.0]])]});}
            var Q52;
            {var subQ6=sQuery(id+"F0.wireOp",EDGE,"E144.MirrorCS");Q52=makeQuery(id+"F0.imprint","IMPRINT",FACE,{"disambiguationData":[TD([[makeQuery(id+"F0.imprint","IMPRINT",EDGE,{"derivedFrom":subQ6}),1.0]])]});}
            var Q53;
            {var subQ0=sQuery(id+"F0.wireOp",EDGE,"E144.MirrorCS");Q53=makeQuery(id+"F0.imprint","IMPRINT",FACE,{"disambiguationData":[TD([[makeQuery(id+"F0.imprint","IMPRINT",EDGE,{"derivedFrom":subQ0}),-1.0]])]});}
            var Q54;
            {var subQ0=sQuery(id+"F0.wireOp",EDGE,"E127.MirrorCS");Q54=makeQuery(id+"F0.imprint","IMPRINT",FACE,{"disambiguationData":[TD([[makeQuery(id+"F0.imprint","IMPRINT",EDGE,{"derivedFrom":subQ0}),-1.0]])]});}
            var Q55;
            {var subQ0=sQuery(id+"F0.wireOp",EDGE,"E127.MirrorCS");Q55=makeQuery(id+"F0.imprint","IMPRINT",FACE,{"disambiguationData":[TD([[makeQuery(id+"F0.imprint","IMPRINT",EDGE,{"derivedFrom":subQ0}),1.0]])]});}
            var Q56;
            {var subQ0=sQuery(id+"F0.wireOp",EDGE,"E89");Q56=makeQuery(id+"F0.imprint","IMPRINT",FACE,{"disambiguationData":[TD([[makeQuery(id+"F0.imprint","IMPRINT",EDGE,{"derivedFrom":subQ0}),-1.0]])]});}
            var Q57;
            {var subQ0=sQuery(id+"F0.wireOp",EDGE,"E180.MirrorCS");var subQ1=sQuery(id+"F0.wireOp",EDGE,"E121.MirrorCS");var subQ2=makeQuery(id+"F0.imprint","INTERSECT",VERTEX,{"derivedFrom":[subQ1,subQ0]});Q57=makeQuery(id+"F0.imprint","IMPRINT",FACE,{"disambiguationData":[TD([[makeQuery(id+"F0.imprint","IMPRINT",EDGE,{"disambiguationData":[TD([[subQ2,-1.0]])],"derivedFrom":subQ0}),1.0]])]});}
            var Q58;
            {var subQ10=sQuery(id+"F0.wireOp",EDGE,"E142.MirrorCS");Q58=makeQuery(id+"F0.imprint","IMPRINT",FACE,{"disambiguationData":[TD([[makeQuery(id+"F0.imprint","IMPRINT",EDGE,{"derivedFrom":subQ10}),1.0]])]});}
            var Q59;
            {var subQ0=sQuery(id+"F0.wireOp",EDGE,"E146.MirrorCS");var subQ1=sQuery(id+"F0.wireOp",EDGE,"E141.MirrorCS");var subQ2=makeQuery(id+"F0.imprint","INTERSECT",VERTEX,{"derivedFrom":[subQ1,subQ0]});Q59=makeQuery(id+"F0.imprint","IMPRINT",FACE,{"disambiguationData":[TD([[makeQuery(id+"F0.imprint","IMPRINT",EDGE,{"disambiguationData":[TD([[subQ2,-1.0]])],"derivedFrom":subQ1}),1.0]])]});}
            var Q60;
            Q60=makeQuery(id+"F0.imprint","IMPRINT",FACE,{"disambiguationData":[TD([[makeQuery(id+"F0.imprint","IMPRINT",EDGE,{"derivedFrom":sQuery(id+"F0.wireOp",EDGE,"E85.MirrorC")}),1.0]])]});
            var Q61;
            {var subQ12=sQuery(id+"F0.wireOp",EDGE,"E187");Q61=makeQuery(id+"F0.imprint","IMPRINT",FACE,{"disambiguationData":[TD([[makeQuery(id+"F0.imprint","IMPRINT",EDGE,{"derivedFrom":subQ12}),-1.0]])]});}
            var Q62;
            {var subQ0=sQuery(id+"F0.wireOp",EDGE,"E137.MirrorCS");Q62=makeQuery(id+"F0.imprint","IMPRINT",FACE,{"disambiguationData":[TD([[makeQuery(id+"F0.imprint","IMPRINT",EDGE,{"derivedFrom":subQ0}),-1.0]])]});}
            var Q63;
            {var subQ0=sQuery(id+"F0.wireOp",EDGE,"E193");Q63=makeQuery(id+"F0.imprint","IMPRINT",FACE,{"disambiguationData":[TD([[makeQuery(id+"F0.imprint","IMPRINT",EDGE,{"derivedFrom":subQ0}),-1.0]])]});}
            var Q64;
            {var subQ0=sQuery(id+"F0.wireOp",EDGE,"E194");Q64=makeQuery(id+"F0.imprint","IMPRINT",FACE,{"disambiguationData":[TD([[makeQuery(id+"F0.imprint","IMPRINT",EDGE,{"derivedFrom":subQ0}),1.0]])]});}
            var Q65;
            {var subQ3=sQuery(id+"F0.wireOp",EDGE,"E49.right");var subQ6=makeQuery(id+"F0.imprint","INTERSECT",VERTEX,{"derivedFrom":[subQ3,sQuery(id+"F0.wireOp",EDGE,"E52")]});Q65=makeQuery(id+"F0.imprint","IMPRINT",FACE,{"disambiguationData":[TD([[makeQuery(id+"F0.imprint","IMPRINT",EDGE,{"disambiguationData":[TD([[subQ6,1.0]])],"derivedFrom":subQ3}),1.0]])]});}
            var Q66;
            {var subQ6=sQuery(id+"F0.wireOp",EDGE,"E141.MirrorCS");var subQ8=makeQuery(id+"F0.imprint","INTERSECT",VERTEX,{"derivedFrom":[subQ6,sQuery(id+"F0.wireOp",EDGE,"E146.MirrorCS")]});Q66=makeQuery(id+"F0.imprint","IMPRINT",FACE,{"disambiguationData":[TD([[makeQuery(id+"F0.imprint","IMPRINT",EDGE,{"disambiguationData":[TD([[subQ8,-1.0]])],"derivedFrom":subQ6}),-1.0]])]});}
            var Q67;
            {var subQ3=sQuery(id+"F0.wireOp",EDGE,"E247");Q67=makeQuery(id+"F0.imprint","IMPRINT",FACE,{"disambiguationData":[TD([[makeQuery(id+"F0.imprint","IMPRINT",EDGE,{"derivedFrom":subQ3}),-1.0]])]});}
            var Q68;
            {var subQ0=sQuery(id+"F0.wireOp",EDGE,"E248");Q68=makeQuery(id+"F0.imprint","IMPRINT",FACE,{"disambiguationData":[TD([[makeQuery(id+"F0.imprint","IMPRINT",EDGE,{"derivedFrom":subQ0}),-1.0]])]});}
            var Q69;
            {var subQ0=sQuery(id+"F0.wireOp",EDGE,"E250");Q69=makeQuery(id+"F0.imprint","IMPRINT",FACE,{"disambiguationData":[TD([[makeQuery(id+"F0.imprint","IMPRINT",EDGE,{"derivedFrom":subQ0}),-1.0]])]});}
            var Q70;
            {var subQ3=sQuery(id+"F0.wireOp",EDGE,"E252");Q70=makeQuery(id+"F0.imprint","IMPRINT",FACE,{"disambiguationData":[TD([[makeQuery(id+"F0.imprint","IMPRINT",EDGE,{"derivedFrom":subQ3}),-1.0]])]});}
            var Q71;
            {var subQ3=sQuery(id+"F0.wireOp",EDGE,"E31");var subQ9=sQuery(id+"F0.wireOp",EDGE,"E16.bottom");var subQ11=makeQuery(id+"F0.imprint","INTERSECT",VERTEX,{"derivedFrom":[subQ9,subQ3]});Q71=makeQuery(id+"F0.imprint","IMPRINT",FACE,{"disambiguationData":[TD([[makeQuery(id+"F0.imprint","IMPRINT",EDGE,{"disambiguationData":[TD([[subQ11,-1.0]])],"derivedFrom":subQ9}),-1.0]])]});}
            var Q72;
            {var subQ0=sQuery(id+"F0.wireOp",EDGE,"E237");var subQ1=sQuery(id+"F0.wireOp",EDGE,"E16.bottom");var subQ2=makeQuery(id+"F0.imprint","INTERSECT",VERTEX,{"derivedFrom":[subQ1,subQ0]});Q72=makeQuery(id+"F0.imprint","IMPRINT",FACE,{"disambiguationData":[TD([[makeQuery(id+"F0.imprint","IMPRINT",EDGE,{"disambiguationData":[TD([[subQ2,-1.0]])],"derivedFrom":subQ0}),1.0]])]});}
            var Q73;
            {var subQ5=sQuery(id+"F0.wireOp",EDGE,"E172.MirrorCS");var subQ7=sQuery(id+"F0.wireOp",EDGE,"E236");var subQ8=makeQuery(id+"F0.imprint","INTERSECT",VERTEX,{"derivedFrom":[subQ5,subQ7]});Q73=makeQuery(id+"F0.imprint","IMPRINT",FACE,{"disambiguationData":[TD([[makeQuery(id+"F0.imprint","IMPRINT",EDGE,{"disambiguationData":[TD([[subQ8,-1.0]])],"derivedFrom":subQ7}),-1.0]])]});}
            var Q74;
            {var subQ1=sQuery(id+"F0.wireOp",EDGE,"E99.MirrorCS");var subQ6=sQuery(id+"F0.wireOp",EDGE,"E165.MirrorCS");var subQ10=makeQuery(id+"F0.imprint","INTERSECT",VERTEX,{"derivedFrom":[subQ1,subQ6]});Q74=makeQuery(id+"F0.imprint","IMPRINT",FACE,{"disambiguationData":[TD([[makeQuery(id+"F0.imprint","IMPRINT",EDGE,{"disambiguationData":[TD([[subQ10,-1.0]])],"derivedFrom":subQ1}),1.0]])]});}
            var Q75;
            {var subQ0=sQuery(id+"F0.wireOp",EDGE,"E210");var subQ5=sQuery(id+"F0.wireOp",EDGE,"E177.MirrorCS");var subQ6=makeQuery(id+"F0.imprint","INTERSECT",VERTEX,{"derivedFrom":[subQ5,subQ0]});Q75=makeQuery(id+"F0.imprint","IMPRINT",FACE,{"disambiguationData":[TD([[makeQuery(id+"F0.imprint","IMPRINT",EDGE,{"disambiguationData":[TD([[subQ6,-1.0]])],"derivedFrom":subQ5}),-1.0]])]});}
            var Q76;
            {var subQ0=sQuery(id+"F0.wireOp",EDGE,"E211");var subQ10=sQuery(id+"F0.wireOp",EDGE,"E49.top");var subQ11=makeQuery(id+"F0.imprint","INTERSECT",VERTEX,{"derivedFrom":[subQ10,subQ0]});Q76=makeQuery(id+"F0.imprint","IMPRINT",FACE,{"disambiguationData":[TD([[makeQuery(id+"F0.imprint","IMPRINT",EDGE,{"disambiguationData":[TD([[subQ11,-1.0]])],"derivedFrom":subQ10}),1.0]])]});}
            var Q77;
            {var subQ0=sQuery(id+"F0.wireOp",EDGE,"E16.top");var subQ5=sQuery(id+"F0.wireOp",EDGE,"E237");var subQ6=makeQuery(id+"F0.imprint","INTERSECT",VERTEX,{"derivedFrom":[subQ0,subQ5]});Q77=makeQuery(id+"F0.imprint","IMPRINT",FACE,{"disambiguationData":[TD([[makeQuery(id+"F0.imprint","IMPRINT",EDGE,{"disambiguationData":[TD([[subQ6,-1.0]])],"derivedFrom":subQ5}),1.0]])]});}
            var Q78;
            {var subQ0=sQuery(id+"F0.wireOp",EDGE,"E173.MirrorCS");var subQ5=sQuery(id+"F0.wireOp",EDGE,"E236");var subQ6=makeQuery(id+"F0.imprint","INTERSECT",VERTEX,{"derivedFrom":[subQ0,subQ5]});Q78=makeQuery(id+"F0.imprint","IMPRINT",FACE,{"disambiguationData":[TD([[makeQuery(id+"F0.imprint","IMPRINT",EDGE,{"disambiguationData":[TD([[subQ6,-1.0]])],"derivedFrom":subQ5}),-1.0]])]});}
            var Q79;
            {var subQ0=sQuery(id+"F0.wireOp",EDGE,"E172.MirrorCS");var subQ5=sQuery(id+"F0.wireOp",EDGE,"E236");var subQ7=makeQuery(id+"F0.imprint","INTERSECT",VERTEX,{"derivedFrom":[subQ0,subQ5]});Q79=makeQuery(id+"F0.imprint","IMPRINT",FACE,{"disambiguationData":[TD([[makeQuery(id+"F0.imprint","IMPRINT",EDGE,{"disambiguationData":[TD([[subQ7,1.0]])],"derivedFrom":subQ5}),-1.0]])]});}
            var Q80;
            {var subQ0=sQuery(id+"F0.wireOp",EDGE,"E16.bottom");var subQ5=sQuery(id+"F0.wireOp",EDGE,"E237");var subQ6=makeQuery(id+"F0.imprint","INTERSECT",VERTEX,{"derivedFrom":[subQ0,subQ5]});Q80=makeQuery(id+"F0.imprint","IMPRINT",FACE,{"disambiguationData":[TD([[makeQuery(id+"F0.imprint","IMPRINT",EDGE,{"disambiguationData":[TD([[subQ6,1.0]])],"derivedFrom":subQ5}),1.0]])]});}
            var Q81;
            {var subQ1=sQuery(id+"F0.wireOp",EDGE,"E20");var subQ3=sQuery(id+"F0.wireOp",EDGE,"E237");var subQ4=makeQuery(id+"F0.imprint","INTERSECT",VERTEX,{"derivedFrom":[subQ1,subQ3]});Q81=makeQuery(id+"F0.imprint","IMPRINT",FACE,{"disambiguationData":[TD([[makeQuery(id+"F0.imprint","IMPRINT",EDGE,{"disambiguationData":[TD([[subQ4,1.0]])],"derivedFrom":subQ3}),1.0]])]});}
            var Q82;
            {var subQ1=sQuery(id+"F0.wireOp",EDGE,"E21");var subQ3=sQuery(id+"F0.wireOp",EDGE,"E237");var subQ4=makeQuery(id+"F0.imprint","INTERSECT",VERTEX,{"derivedFrom":[subQ1,subQ3]});Q82=makeQuery(id+"F0.imprint","IMPRINT",FACE,{"disambiguationData":[TD([[makeQuery(id+"F0.imprint","IMPRINT",EDGE,{"disambiguationData":[TD([[subQ4,-1.0]])],"derivedFrom":subQ3}),1.0]])]});}
            var Q83;
            {var subQ1=sQuery(id+"F0.wireOp",EDGE,"E174.MirrorCS");var subQ3=sQuery(id+"F0.wireOp",EDGE,"E236");var subQ4=makeQuery(id+"F0.imprint","INTERSECT",VERTEX,{"derivedFrom":[subQ1,subQ3]});Q83=makeQuery(id+"F0.imprint","IMPRINT",FACE,{"disambiguationData":[TD([[makeQuery(id+"F0.imprint","IMPRINT",EDGE,{"disambiguationData":[TD([[subQ4,-1.0]])],"derivedFrom":subQ3}),-1.0]])]});}
            var Q84;
            {var subQ1=sQuery(id+"F0.wireOp",EDGE,"E174.MirrorCS");var subQ3=sQuery(id+"F0.wireOp",EDGE,"E236");var subQ4=makeQuery(id+"F0.imprint","INTERSECT",VERTEX,{"derivedFrom":[subQ1,subQ3]});Q84=makeQuery(id+"F0.imprint","IMPRINT",FACE,{"disambiguationData":[TD([[makeQuery(id+"F0.imprint","IMPRINT",EDGE,{"disambiguationData":[TD([[subQ4,1.0]])],"derivedFrom":subQ3}),-1.0]])]});}
            var Q85;
            {var subQ0=sQuery(id+"F0.wireOp",EDGE,"E249");Q85=makeQuery(id+"F0.imprint","IMPRINT",FACE,{"disambiguationData":[TD([[makeQuery(id+"F0.imprint","IMPRINT",EDGE,{"derivedFrom":subQ0}),-1.0]])]});}
            var Q86;
            {var subQ0=sQuery(id+"F0.wireOp",EDGE,"E251");Q86=makeQuery(id+"F0.imprint","IMPRINT",FACE,{"disambiguationData":[TD([[makeQuery(id+"F0.imprint","IMPRINT",EDGE,{"derivedFrom":subQ0}),-1.0]])]});}
            var Q87;
            {var subQ5=sQuery(id+"F0.wireOp",EDGE,"E264.trimOffspring");Q87=makeQuery(id+"F0.imprint","IMPRINT",FACE,{"disambiguationData":[TD([[makeQuery(id+"F0.imprint","IMPRINT",EDGE,{"derivedFrom":subQ5}),-1.0]])]});}
            var Q88;
            {var subQ9=sQuery(id+"F0.wireOp",EDGE,"E210");Q88=makeQuery(id+"F0.imprint","IMPRINT",FACE,{"disambiguationData":[TD([[makeQuery(id+"F0.imprint","IMPRINT",EDGE,{"derivedFrom":subQ9}),-1.0]])]});}
            var Q89;
            {var subQ2=sQuery(id+"F0.wireOp",EDGE,"E262.trimOffspring");Q89=makeQuery(id+"F0.imprint","IMPRINT",FACE,{"disambiguationData":[TD([[makeQuery(id+"F0.imprint","IMPRINT",EDGE,{"derivedFrom":subQ2}),1.0]])]});}
            var Q90;
            {var subQ0=sQuery(id+"F0.wireOp",EDGE,"E211");Q90=makeQuery(id+"F0.imprint","IMPRINT",FACE,{"disambiguationData":[TD([[makeQuery(id+"F0.imprint","IMPRINT",EDGE,{"derivedFrom":subQ0}),-1.0]])]});}
            extrude(context, id + "F1", {"entities" : qUnion([Q0, Q1, Q2, Q3, Q4, Q5, Q6, Q7, Q8, Q9, Q10, Q11, Q12, Q13, Q14, Q15, Q16, Q17, Q18, Q19, Q20, Q21, Q22, Q23, Q24, Q25, Q26, Q27, Q28, Q29, Q30, Q31, Q32, Q33, Q34, Q35, Q36, Q37, Q38, Q39, Q40, Q41, Q42, Q43, Q44, Q45, Q46, Q47, Q48, Q49, Q50, Q51, Q52, Q53, Q54, Q55, Q56, Q57, Q58, Q59, Q60, Q61, Q62, Q63, Q64, Q65, Q66, Q67, Q68, Q69, Q70, Q71, Q72, Q73, Q74, Q75, Q76, Q77, Q78, Q79, Q80, Q81, Q82, Q83, Q84, Q85, Q86, Q87, Q88, Q89, Q90]), "depth" : 3 * mm});
        }
    });
